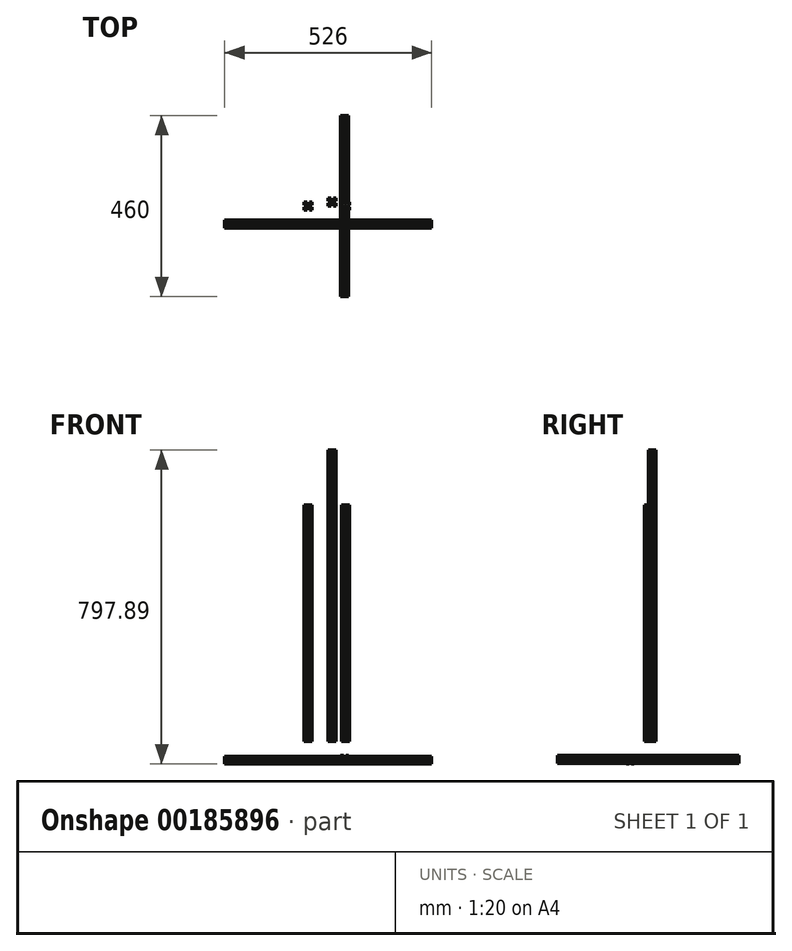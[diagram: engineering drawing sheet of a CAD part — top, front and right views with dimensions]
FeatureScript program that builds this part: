
annotation { "Feature Type Name" : "Feature", "Feature Type Description" : "" }
export const myFeature = defineFeature(function(context is Context, id is Id, definition is map)
    precondition{}
    {
        {
            var Q0;
            Q0=qCreatedBy(makeId("Top.planeOp"),FACE);
            var sketch = newSketch(context, id + "F0", { "sketchPlane" : qUnion([Q0])});
            skLineSegment(sketch, "E0.bottom", {"start": v(0, 0) * mm, "end": v(20, 0) * mm});
            skLineSegment(sketch, "E0.top", {"start": v(0, 20) * mm, "end": v(20, 20) * mm});
            skLineSegment(sketch, "E0.left", {"start": v(0, 0) * mm, "end": v(0, 20) * mm});
            skLineSegment(sketch, "E0.right", {"start": v(20, 0) * mm, "end": v(20, 20) * mm});
            skLineSegment(sketch, "E1.bottom", {"start": v(7, 20) * mm, "end": v(13, 20) * mm});
            skLineSegment(sketch, "E1.top", {"start": v(7, 14.5) * mm, "end": v(13, 14.5) * mm});
            skLineSegment(sketch, "E1.left", {"start": v(7, 20) * mm, "end": v(7, 14.5) * mm});
            skLineSegment(sketch, "E1.right", {"start": v(13, 20) * mm, "end": v(13, 14.5) * mm});
            skLineSegment(sketch, "E2.bottom", {"start": v(20, 13) * mm, "end": v(14.5, 13) * mm});
            skLineSegment(sketch, "E2.top", {"start": v(20, 7) * mm, "end": v(14.5, 7) * mm});
            skLineSegment(sketch, "E2.left", {"start": v(20, 13) * mm, "end": v(20, 7) * mm});
            skLineSegment(sketch, "E2.right", {"start": v(14.5, 13) * mm, "end": v(14.5, 7) * mm});
            skLineSegment(sketch, "E3.bottom", {"start": v(13, 0) * mm, "end": v(7, 0) * mm});
            skLineSegment(sketch, "E3.top", {"start": v(13, 5.5) * mm, "end": v(7, 5.5) * mm});
            skLineSegment(sketch, "E3.left", {"start": v(13, 0) * mm, "end": v(13, 5.5) * mm});
            skLineSegment(sketch, "E3.right", {"start": v(7, 0) * mm, "end": v(7, 5.5) * mm});
            skLineSegment(sketch, "E4.bottom", {"start": v(0, 7) * mm, "end": v(5.5, 7) * mm});
            skLineSegment(sketch, "E4.top", {"start": v(0, 13) * mm, "end": v(5.5, 13) * mm});
            skLineSegment(sketch, "E4.left", {"start": v(0, 7) * mm, "end": v(0, 13) * mm});
            skLineSegment(sketch, "E4.right", {"start": v(5.5, 7) * mm, "end": v(5.5, 13) * mm});
            skSolve(sketch);
        }
        {
            var Q0;
            Q0=makeQuery(id+"F0.imprint","IMPRINT",FACE,{"disambiguationData":[TD([[makeQuery(id+"F0.imprint","IMPRINT",EDGE,{"derivedFrom":sQuery(id+"F0.wireOp",EDGE,"E1.top")}),-1.0]])]});
            extrude(context, id + "F1", {"entities" : qUnion([Q0]), "depth" : 740 * mm});
        }
        {
            var Q0;
            Q0=qCreatedBy(makeId("Top.planeOp"),FACE);
            var sketch = newSketch(context, id + "F2", { "sketchPlane" : qUnion([Q0])});
            skLineSegment(sketch, "E5.bottom", {"start": v(-61, -10) * mm, "end": v(-41, -10) * mm});
            skLineSegment(sketch, "E5.top", {"start": v(-61, 10) * mm, "end": v(-41, 10) * mm});
            skLineSegment(sketch, "E5.left", {"start": v(-61, -10) * mm, "end": v(-61, 10) * mm});
            skLineSegment(sketch, "E5.right", {"start": v(-41, -10) * mm, "end": v(-41, 10) * mm});
            skLineSegment(sketch, "E6.top", {"start": v(-54, 4.5) * mm, "end": v(-48, 4.5) * mm});
            skLineSegment(sketch, "E6.left", {"start": v(-54, 10) * mm, "end": v(-54, 4.5) * mm});
            skLineSegment(sketch, "E6.right", {"start": v(-48, 10) * mm, "end": v(-48, 4.5) * mm});
            skLineSegment(sketch, "E7.bottom", {"start": v(-41, 3) * mm, "end": v(-46.5, 3) * mm});
            skLineSegment(sketch, "E7.top", {"start": v(-41, -3) * mm, "end": v(-46.5, -3) * mm});
            skLineSegment(sketch, "E7.left", {"start": v(-41, 3) * mm, "end": v(-41, -3) * mm});
            skLineSegment(sketch, "E7.right", {"start": v(-46.5, 3) * mm, "end": v(-46.5, -3) * mm});
            skLineSegment(sketch, "E8.top", {"start": v(-48, -4.5) * mm, "end": v(-54, -4.5) * mm});
            skLineSegment(sketch, "E8.left", {"start": v(-48, -10) * mm, "end": v(-48, -4.5) * mm});
            skLineSegment(sketch, "E8.right", {"start": v(-54, -10) * mm, "end": v(-54, -4.5) * mm});
            skLineSegment(sketch, "E9.bottom", {"start": v(-61, -3) * mm, "end": v(-55.5, -3) * mm});
            skLineSegment(sketch, "E9.top", {"start": v(-61, 3) * mm, "end": v(-55.5, 3) * mm});
            skLineSegment(sketch, "E9.left", {"start": v(-61, -3) * mm, "end": v(-61, 3) * mm});
            skLineSegment(sketch, "E9.right", {"start": v(-55.5, -3) * mm, "end": v(-55.5, 3) * mm});
            skSolve(sketch);
        }
        {
            var Q0;
            Q0=makeQuery(id+"F2.imprint","IMPRINT",FACE,{"disambiguationData":[TD([[makeQuery(id+"F2.imprint","IMPRINT",EDGE,{"derivedFrom":sQuery(id+"F2.wireOp",EDGE,"E6.top")}),-1.0]])]});
            extrude(context, id + "F3", {"entities" : qUnion([Q0]), "depth" : 600 * mm});
        }
        {
            var Q0;
            Q0=qCreatedBy(makeId("Top.planeOp"),FACE);
            var sketch = newSketch(context, id + "F4", { "sketchPlane" : qUnion([Q0])});
            skLineSegment(sketch, "E10.bottom", {"start": v(34, -10) * mm, "end": v(54, -10) * mm});
            skLineSegment(sketch, "E10.top", {"start": v(34, 10) * mm, "end": v(54, 10) * mm});
            skLineSegment(sketch, "E10.left", {"start": v(34, -10) * mm, "end": v(34, 10) * mm});
            skLineSegment(sketch, "E10.right", {"start": v(54, -10) * mm, "end": v(54, 10) * mm});
            skLineSegment(sketch, "E11.bottom", {"start": v(41, 10) * mm, "end": v(47, 10) * mm});
            skLineSegment(sketch, "E11.top", {"start": v(41, 4.5) * mm, "end": v(47, 4.5) * mm});
            skLineSegment(sketch, "E11.left", {"start": v(41, 10) * mm, "end": v(41, 4.5) * mm});
            skLineSegment(sketch, "E11.right", {"start": v(47, 10) * mm, "end": v(47, 4.5) * mm});
            skLineSegment(sketch, "E12.bottom", {"start": v(54, 3) * mm, "end": v(48.5, 3) * mm});
            skLineSegment(sketch, "E12.top", {"start": v(54, -3) * mm, "end": v(48.5, -3) * mm});
            skLineSegment(sketch, "E12.left", {"start": v(54, 3) * mm, "end": v(54, -3) * mm});
            skLineSegment(sketch, "E12.right", {"start": v(48.5, 3) * mm, "end": v(48.5, -3) * mm});
            skLineSegment(sketch, "E13.bottom", {"start": v(47, -10) * mm, "end": v(41, -10) * mm});
            skLineSegment(sketch, "E13.top", {"start": v(47, -4.5) * mm, "end": v(41, -4.5) * mm});
            skLineSegment(sketch, "E13.left", {"start": v(47, -10) * mm, "end": v(47, -4.5) * mm});
            skLineSegment(sketch, "E13.right", {"start": v(41, -10) * mm, "end": v(41, -4.5) * mm});
            skLineSegment(sketch, "E14.bottom", {"start": v(34, -3) * mm, "end": v(39.5, -3) * mm});
            skLineSegment(sketch, "E14.top", {"start": v(34, 3) * mm, "end": v(39.5, 3) * mm});
            skLineSegment(sketch, "E14.left", {"start": v(34, -3) * mm, "end": v(34, 3) * mm});
            skLineSegment(sketch, "E14.right", {"start": v(39.5, -3) * mm, "end": v(39.5, 3) * mm});
            skSolve(sketch);
        }
        {
            var Q0;
            Q0=makeQuery(id+"F4.imprint","IMPRINT",FACE,{"disambiguationData":[TD([[makeQuery(id+"F4.imprint","IMPRINT",EDGE,{"derivedFrom":sQuery(id+"F4.wireOp",EDGE,"E11.top")}),-1.0]])]});
            extrude(context, id + "F5", {"entities" : qUnion([Q0]), "depth" : 600 * mm});
        }
        {
            var Q0;
            Q0=qCreatedBy(makeId("Right.planeOp"),FACE);
            var sketch = newSketch(context, id + "F6", { "sketchPlane" : qUnion([Q0])});
            skLineSegment(sketch, "E15.bottom", {"start": v(-55.88, -57.89) * mm, "end": v(-35.88, -57.89) * mm});
            skLineSegment(sketch, "E15.top", {"start": v(-55.88, -37.89) * mm, "end": v(-35.88, -37.89) * mm});
            skLineSegment(sketch, "E15.left", {"start": v(-55.88, -57.89) * mm, "end": v(-55.88, -37.89) * mm});
            skLineSegment(sketch, "E15.right", {"start": v(-35.88, -57.89) * mm, "end": v(-35.88, -37.89) * mm});
            skLineSegment(sketch, "E16.bottom", {"start": v(-48.88, -37.89) * mm, "end": v(-42.88, -37.89) * mm});
            skLineSegment(sketch, "E16.top", {"start": v(-48.88, -43.39) * mm, "end": v(-42.88, -43.39) * mm});
            skLineSegment(sketch, "E16.left", {"start": v(-48.88, -37.89) * mm, "end": v(-48.88, -43.39) * mm});
            skLineSegment(sketch, "E16.right", {"start": v(-42.88, -37.89) * mm, "end": v(-42.88, -43.39) * mm});
            skLineSegment(sketch, "E17.bottom", {"start": v(-35.88, -44.89) * mm, "end": v(-41.38, -44.89) * mm});
            skLineSegment(sketch, "E17.top", {"start": v(-35.88, -50.89) * mm, "end": v(-41.38, -50.89) * mm});
            skLineSegment(sketch, "E17.left", {"start": v(-35.88, -44.89) * mm, "end": v(-35.88, -50.89) * mm});
            skLineSegment(sketch, "E17.right", {"start": v(-41.38, -44.89) * mm, "end": v(-41.38, -50.89) * mm});
            skLineSegment(sketch, "E18.bottom", {"start": v(-42.88, -57.89) * mm, "end": v(-48.88, -57.89) * mm});
            skLineSegment(sketch, "E18.top", {"start": v(-42.88, -52.39) * mm, "end": v(-48.88, -52.39) * mm});
            skLineSegment(sketch, "E18.left", {"start": v(-42.88, -57.89) * mm, "end": v(-42.88, -52.39) * mm});
            skLineSegment(sketch, "E18.right", {"start": v(-48.88, -57.89) * mm, "end": v(-48.88, -52.39) * mm});
            skLineSegment(sketch, "E19.bottom", {"start": v(-55.88, -50.89) * mm, "end": v(-50.38, -50.89) * mm});
            skLineSegment(sketch, "E19.top", {"start": v(-55.88, -44.89) * mm, "end": v(-50.38, -44.89) * mm});
            skLineSegment(sketch, "E19.left", {"start": v(-55.88, -50.89) * mm, "end": v(-55.88, -44.89) * mm});
            skLineSegment(sketch, "E19.right", {"start": v(-50.38, -50.89) * mm, "end": v(-50.38, -44.89) * mm});
            skSolve(sketch);
        }
        {
            var Q0;
            Q0=makeQuery(id+"F6.imprint","IMPRINT",FACE,{"disambiguationData":[TD([[makeQuery(id+"F6.imprint","IMPRINT",EDGE,{"derivedFrom":sQuery(id+"F6.wireOp",EDGE,"E16.top")}),-1.0]])]});
            extrude(context, id + "F7", {"entities" : qUnion([Q0]), "endBound" : BoundingType.SYMMETRIC, "depth" : 526 * mm});
        }
        {
            var Q0;
            Q0=qCreatedBy(makeId("Front.planeOp"),FACE);
            var sketch = newSketch(context, id + "F8", { "sketchPlane" : qUnion([Q0])});
            skLineSegment(sketch, "E20.bottom", {"start": v(31.6, -56.3) * mm, "end": v(51.6, -56.3) * mm});
            skLineSegment(sketch, "E20.top", {"start": v(31.6, -36.3) * mm, "end": v(51.6, -36.3) * mm});
            skLineSegment(sketch, "E20.left", {"start": v(31.6, -56.3) * mm, "end": v(31.6, -36.3) * mm});
            skLineSegment(sketch, "E20.right", {"start": v(51.6, -56.3) * mm, "end": v(51.6, -36.3) * mm});
            skLineSegment(sketch, "E21.bottom", {"start": v(38.6, -36.3) * mm, "end": v(44.6, -36.3) * mm});
            skLineSegment(sketch, "E21.top", {"start": v(38.6, -41.8) * mm, "end": v(44.6, -41.8) * mm});
            skLineSegment(sketch, "E21.left", {"start": v(38.6, -36.3) * mm, "end": v(38.6, -41.8) * mm});
            skLineSegment(sketch, "E21.right", {"start": v(44.6, -36.3) * mm, "end": v(44.6, -41.8) * mm});
            skLineSegment(sketch, "E22.bottom", {"start": v(51.6, -43.3) * mm, "end": v(46.1, -43.3) * mm});
            skLineSegment(sketch, "E22.top", {"start": v(51.6, -49.3) * mm, "end": v(46.1, -49.3) * mm});
            skLineSegment(sketch, "E22.left", {"start": v(51.6, -43.3) * mm, "end": v(51.6, -49.3) * mm});
            skLineSegment(sketch, "E22.right", {"start": v(46.1, -43.3) * mm, "end": v(46.1, -49.3) * mm});
            skLineSegment(sketch, "E23.bottom", {"start": v(44.6, -56.3) * mm, "end": v(38.6, -56.3) * mm});
            skLineSegment(sketch, "E23.top", {"start": v(44.6, -50.8) * mm, "end": v(38.6, -50.8) * mm});
            skLineSegment(sketch, "E23.left", {"start": v(44.6, -56.3) * mm, "end": v(44.6, -50.8) * mm});
            skLineSegment(sketch, "E23.right", {"start": v(38.6, -56.3) * mm, "end": v(38.6, -50.8) * mm});
            skLineSegment(sketch, "E24.bottom", {"start": v(31.6, -49.3) * mm, "end": v(37.1, -49.3) * mm});
            skLineSegment(sketch, "E24.top", {"start": v(31.6, -43.3) * mm, "end": v(37.1, -43.3) * mm});
            skLineSegment(sketch, "E24.left", {"start": v(31.6, -49.3) * mm, "end": v(31.6, -43.3) * mm});
            skLineSegment(sketch, "E24.right", {"start": v(37.1, -49.3) * mm, "end": v(37.1, -43.3) * mm});
            skSolve(sketch);
        }
        {
            var Q0;
            Q0=makeQuery(id+"F8.imprint","IMPRINT",FACE,{"disambiguationData":[TD([[makeQuery(id+"F8.imprint","IMPRINT",EDGE,{"derivedFrom":sQuery(id+"F8.wireOp",EDGE,"E21.top")}),-1.0]])]});
            extrude(context, id + "F9", {"entities" : qUnion([Q0]), "endBound" : BoundingType.SYMMETRIC, "depth" : 460 * mm});
        }
    });
